# Revit family: RHTS7014-H
name_source: partatom
category: Generic Models
units: mm (PartAtom-declared; Revit-internal decimal feet)

## family parameters
Always vertical = No
Can host rebar = No
Cut with Voids When Loaded = No
Host = Roof
Maintain Annotation Orientation = No
Part Type = Normal
Room Calculation Point = No
Round Connector Dimension = Use Diameter
Shared = No

## types (1)
- RHTS7014-H
    Ceiling height = 3500 mm
    Clamps mat. = Steel
    Cradle mat. = Multiplex
    Default Elevation = 0 mm  [stored 0 ft]
    Depth = 1500 mm  [stored 4.92126 ft]
    Description = Roof access hatch with folding stairs
    Gripp mat. = Poly
    Lid mat. = Plastic
    Manufacturer = https://www.gortergroup.com
    Model = RHTS1015-H
    Railing Left = Yes
    Railing Right = Yes
    Rim mat. = Plastic
    Seal mat. = Rubber
    Staircase Unfolded = No
    Stinger mat. = Aluminium
    URL = https://www.gortergroup.com
    Wheels mat. = Poly
    Width = 1000 mm  [stored 3.28084 ft]

note: [stored X ft] marks values corroborated as IEEE doubles in the binary element streams (Revit-internal decimal feet)

## geometry (parser evidence)
native form markers: Sweep x59
no freeform markers — native parametric forms only
